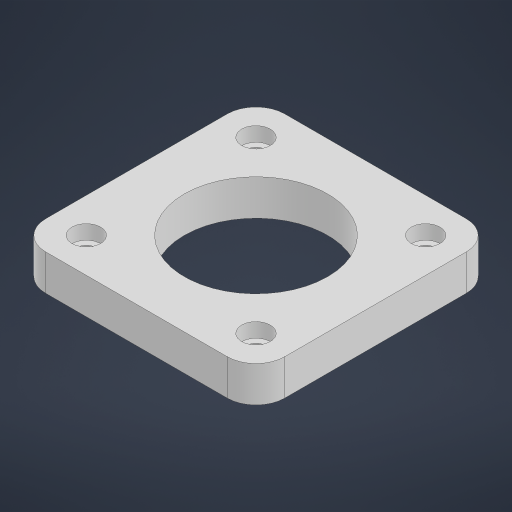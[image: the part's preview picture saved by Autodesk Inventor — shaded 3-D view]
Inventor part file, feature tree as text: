
AUTODESK INVENTOR PART (.ipt)
format: ipt  version: 2024.1 (Build 281209000, 209)  size: 196,608 bytes
history: native  units: mm
features: sketch x1, extrude x1, hole x1, fillet x1
ambient origin geometry x8: Origin, YZ Plane, XZ Plane, XY Plane, X Axis, Y Axis, Z Axis, Center Point
bodies: Solid1 (feature_tree)
feature tree (4):
  sketch  "Sketch1"  dims[d0=100.0mm d1=60.0mm d2=71.0mm d3=15.0mm d4=0.0mm d5=7.0mm d6=7.0mm d7=12.0mm d8=6.0mm d9=90.0deg d10=8.0mm d11=20.594885mm d12=12.0mm d13=100.409163mm]
  extrude  "Extrusion1"  Depth=12.0mm
  hole  "Hole1"  [1 undecoded]
  fillet  "Fillet1"  Radius=15.0mm
note: 1 required parameter value undecoded (feature->parameter linkage not recoverable at this tier; creation-order binding heuristic only, values carry confidence <= 0.55)
